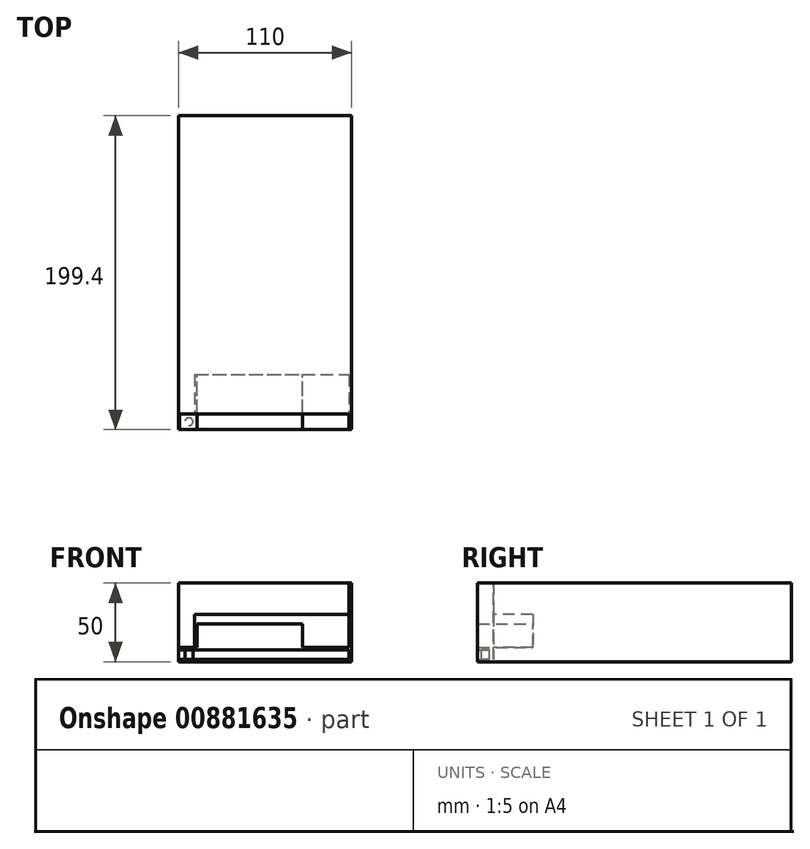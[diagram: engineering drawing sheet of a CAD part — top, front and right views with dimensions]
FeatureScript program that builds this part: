
annotation { "Feature Type Name" : "Feature", "Feature Type Description" : "" }
export const myFeature = defineFeature(function(context is Context, id is Id, definition is map)
    precondition{}
    {
        {
            var Q0;
            Q0=qCreatedBy(makeId("Front.planeOp"),FACE);
            var sketch = newSketch(context, id + "F0", { "sketchPlane" : qUnion([Q0])});
            skLineSegment(sketch, "E0.bottom", {"start": v(0, 0) * mm, "end": v(110, 0) * mm});
            skLineSegment(sketch, "E0.top", {"start": v(0, 50) * mm, "end": v(110, 50) * mm});
            skLineSegment(sketch, "E0.left", {"start": v(0, 0) * mm, "end": v(0, 50) * mm});
            skLineSegment(sketch, "E0.right", {"start": v(110, 0) * mm, "end": v(110, 50) * mm});
            skLineSegment(sketch, "E1", {"start": v(108.4, 50) * mm, "end": v(108.4, 0) * mm});
            skLineSegment(sketch, "E2", {"start": v(0, 9.2) * mm, "end": v(108.4, 9.2) * mm});
            skLineSegment(sketch, "E3", {"start": v(10.2, 50) * mm, "end": v(10.2, 9.2) * mm});
            skLineSegment(sketch, "E4", {"start": v(10.2, 30) * mm, "end": v(108.4, 30) * mm});
            skLineSegment(sketch, "E5", {"start": v(11.6, 9.2) * mm, "end": v(11.6, 24.1) * mm});
            skLineSegment(sketch, "E6", {"start": v(11.6, 24.1) * mm, "end": v(78.8, 24.1) * mm});
            skLineSegment(sketch, "E7", {"start": v(78.8, 24.1) * mm, "end": v(78.8, 9.2) * mm});
            skLineSegment(sketch, "E8", {"start": v(0, 7.6) * mm, "end": v(108.4, 7.6) * mm});
            skLineSegment(sketch, "E9", {"start": v(0, 1.6) * mm, "end": v(108.4, 1.6) * mm});
            skLineSegment(sketch, "E10", {"start": v(0.6, 0) * mm, "end": v(0.6, 50) * mm});
            skLineSegment(sketch, "E11", {"start": v(0, 49.4) * mm, "end": v(110, 49.4) * mm});
            skSolve(sketch);
        }
        {
            var Q0;
            {var subQ0=sQuery(id+"F0.wireOp",EDGE,"E1");var subQ1=sQuery(id+"F0.wireOp",EDGE,"E0.top");var subQ2=makeQuery(id+"F0.imprint","INTERSECT",VERTEX,{"derivedFrom":[subQ1,subQ0]});Q0=makeQuery(id+"F0.imprint","IMPRINT",FACE,{"disambiguationData":[TD([[makeQuery(id+"F0.imprint","IMPRINT",EDGE,{"disambiguationData":[TD([[subQ2,1.0]])],"derivedFrom":subQ1}),-1.0]])]});}
            var Q1;
            {var subQ0=sQuery(id+"F0.wireOp",EDGE,"E3");var subQ1=sQuery(id+"F0.wireOp",EDGE,"E0.top");var subQ2=makeQuery(id+"F0.imprint","INTERSECT",VERTEX,{"derivedFrom":[subQ1,subQ0]});Q1=makeQuery(id+"F0.imprint","IMPRINT",FACE,{"disambiguationData":[TD([[makeQuery(id+"F0.imprint","IMPRINT",EDGE,{"disambiguationData":[TD([[subQ2,1.0]])],"derivedFrom":subQ1}),-1.0]])]});}
            var Q2;
            {var subQ0=sQuery(id+"F0.wireOp",EDGE,"E2");var subQ1=sQuery(id+"F0.wireOp",EDGE,"E0.left");var subQ2=makeQuery(id+"F0.imprint","INTERSECT",VERTEX,{"derivedFrom":[subQ1,subQ0]});Q2=makeQuery(id+"F0.imprint","IMPRINT",FACE,{"disambiguationData":[TD([[makeQuery(id+"F0.imprint","IMPRINT",EDGE,{"disambiguationData":[TD([[subQ2,-1.0]])],"derivedFrom":subQ1}),-1.0]])]});}
            var Q3;
            {var subQ0=sQuery(id+"F0.wireOp",EDGE,"E2");var subQ1=sQuery(id+"F0.wireOp",EDGE,"E0.left");var subQ2=makeQuery(id+"F0.imprint","INTERSECT",VERTEX,{"derivedFrom":[subQ1,subQ0]});Q3=makeQuery(id+"F0.imprint","IMPRINT",FACE,{"disambiguationData":[TD([[makeQuery(id+"F0.imprint","IMPRINT",EDGE,{"disambiguationData":[TD([[subQ2,1.0]])],"derivedFrom":subQ1}),-1.0]])]});}
            var Q4;
            {var subQ0=sQuery(id+"F0.wireOp",EDGE,"E8");var subQ1=sQuery(id+"F0.wireOp",EDGE,"E0.left");var subQ2=makeQuery(id+"F0.imprint","INTERSECT",VERTEX,{"derivedFrom":[subQ1,subQ0]});Q4=makeQuery(id+"F0.imprint","IMPRINT",FACE,{"disambiguationData":[TD([[makeQuery(id+"F0.imprint","IMPRINT",EDGE,{"disambiguationData":[TD([[subQ2,1.0]])],"derivedFrom":subQ1}),-1.0]])]});}
            var Q5;
            {var subQ0=sQuery(id+"F0.wireOp",EDGE,"E0.left");var subQ1=sQuery(id+"F0.wireOp",EDGE,"E0.bottom");var subQ2=makeQuery(id+"F0.imprint","INTERSECT",VERTEX,{"derivedFrom":[subQ1,subQ0]});Q5=makeQuery(id+"F0.imprint","IMPRINT",FACE,{"disambiguationData":[TD([[makeQuery(id+"F0.imprint","IMPRINT",EDGE,{"disambiguationData":[TD([[subQ2,-1.0]])],"derivedFrom":subQ1}),1.0]])]});}
            var Q6;
            {var subQ0=sQuery(id+"F0.wireOp",EDGE,"E1");var subQ1=sQuery(id+"F0.wireOp",EDGE,"E0.bottom");var subQ2=makeQuery(id+"F0.imprint","INTERSECT",VERTEX,{"derivedFrom":[subQ1,subQ0]});Q6=makeQuery(id+"F0.imprint","IMPRINT",FACE,{"disambiguationData":[TD([[makeQuery(id+"F0.imprint","IMPRINT",EDGE,{"disambiguationData":[TD([[subQ2,1.0]])],"derivedFrom":subQ1}),1.0]])]});}
            var Q7;
            {var subQ5=sQuery(id+"F0.wireOp",EDGE,"E0.right");var subQ6=sQuery(id+"F0.wireOp",EDGE,"E0.bottom");var subQ7=makeQuery(id+"F0.imprint","INTERSECT",VERTEX,{"derivedFrom":[subQ6,subQ5]});Q7=makeQuery(id+"F0.imprint","IMPRINT",FACE,{"disambiguationData":[TD([[makeQuery(id+"F0.imprint","IMPRINT",EDGE,{"disambiguationData":[TD([[subQ7,1.0]])],"derivedFrom":subQ6}),1.0]])]});}
            var Q8;
            {var subQ0=sQuery(id+"F0.wireOp",EDGE,"E0.right");var subQ1=sQuery(id+"F0.wireOp",EDGE,"E0.top");var subQ2=makeQuery(id+"F0.imprint","INTERSECT",VERTEX,{"derivedFrom":[subQ1,subQ0]});Q8=makeQuery(id+"F0.imprint","IMPRINT",FACE,{"disambiguationData":[TD([[makeQuery(id+"F0.imprint","IMPRINT",EDGE,{"disambiguationData":[TD([[subQ2,1.0]])],"derivedFrom":subQ1}),-1.0]])]});}
            var Q9;
            {var subQ0=sQuery(id+"F0.wireOp",EDGE,"E0.left");var subQ1=sQuery(id+"F0.wireOp",EDGE,"E0.top");var subQ2=makeQuery(id+"F0.imprint","INTERSECT",VERTEX,{"derivedFrom":[subQ1,subQ0]});Q9=makeQuery(id+"F0.imprint","IMPRINT",FACE,{"disambiguationData":[TD([[makeQuery(id+"F0.imprint","IMPRINT",EDGE,{"disambiguationData":[TD([[subQ2,-1.0]])],"derivedFrom":subQ1}),-1.0]])]});}
            var Q10;
            {var subQ0=sQuery(id+"F0.wireOp",EDGE,"E2");var subQ7=sQuery(id+"F0.wireOp",EDGE,"E1");var subQ10=makeQuery(id+"F0.imprint","INTERSECT",VERTEX,{"derivedFrom":[subQ7,subQ0]});Q10=makeQuery(id+"F0.imprint","IMPRINT",FACE,{"disambiguationData":[TD([[makeQuery(id+"F0.imprint","IMPRINT",EDGE,{"disambiguationData":[TD([[subQ10,-1.0]])],"derivedFrom":subQ7}),-1.0]])]});}
            var Q11;
            {var subQ1=sQuery(id+"F0.wireOp",EDGE,"E2");var subQ5=sQuery(id+"F0.wireOp",EDGE,"E3");var subQ6=makeQuery(id+"F0.imprint","INTERSECT",VERTEX,{"derivedFrom":[subQ1,subQ5]});Q11=makeQuery(id+"F0.imprint","IMPRINT",FACE,{"disambiguationData":[TD([[makeQuery(id+"F0.imprint","IMPRINT",EDGE,{"disambiguationData":[TD([[subQ6,1.0]])],"derivedFrom":subQ1}),1.0]])]});}
            var Q12;
            {var subQ0=sQuery(id+"F0.wireOp",EDGE,"E4");Q12=makeQuery(id+"F0.imprint","IMPRINT",FACE,{"disambiguationData":[TD([[makeQuery(id+"F0.imprint","IMPRINT",EDGE,{"derivedFrom":subQ0}),1.0]])]});}
            var Q13;
            {var subQ6=sQuery(id+"F0.wireOp",EDGE,"E4");Q13=makeQuery(id+"F0.imprint","IMPRINT",FACE,{"disambiguationData":[TD([[makeQuery(id+"F0.imprint","IMPRINT",EDGE,{"derivedFrom":subQ6}),-1.0]])]});}
            var Q14;
            {var subQ0=sQuery(id+"F0.wireOp",EDGE,"E5");Q14=makeQuery(id+"F0.imprint","IMPRINT",FACE,{"disambiguationData":[TD([[makeQuery(id+"F0.imprint","IMPRINT",EDGE,{"derivedFrom":subQ0}),-1.0]])]});}
            var Q15;
            {var subQ0=sQuery(id+"F0.wireOp",EDGE,"E8");var subQ1=sQuery(id+"F0.wireOp",EDGE,"E1");var subQ2=makeQuery(id+"F0.imprint","INTERSECT",VERTEX,{"derivedFrom":[subQ1,subQ0]});Q15=makeQuery(id+"F0.imprint","IMPRINT",FACE,{"disambiguationData":[TD([[makeQuery(id+"F0.imprint","IMPRINT",EDGE,{"disambiguationData":[TD([[subQ2,-1.0]])],"derivedFrom":subQ1}),-1.0]])]});}
            extrude(context, id + "F1", {"entities" : qUnion([Q0, Q1, Q2, Q3, Q4, Q5, Q6, Q7, Q8, Q9, Q10, Q11, Q12, Q13, Q14, Q15]), "oppositeDirection" : true, "depth" : 189.4 * mm, "offsetDistance" : 25 * mm});
        }
        {
            var Q0;
            {var subQ0=sQuery(id+"F0.wireOp",EDGE,"E5");Q0=makeQuery(id+"F0.imprint","IMPRINT",FACE,{"disambiguationData":[TD([[makeQuery(id+"F0.imprint","IMPRINT",EDGE,{"derivedFrom":subQ0}),-1.0]])]});}
            var Q1;
            {var subQ5=sQuery(id+"F0.wireOp",EDGE,"E0.right");var subQ6=sQuery(id+"F0.wireOp",EDGE,"E0.bottom");var subQ7=makeQuery(id+"F0.imprint","INTERSECT",VERTEX,{"derivedFrom":[subQ6,subQ5]});Q1=makeQuery(id+"F0.imprint","IMPRINT",FACE,{"disambiguationData":[TD([[makeQuery(id+"F0.imprint","IMPRINT",EDGE,{"disambiguationData":[TD([[subQ7,1.0]])],"derivedFrom":subQ6}),1.0]])]});}
            var Q2;
            {var subQ0=sQuery(id+"F0.wireOp",EDGE,"E1");var subQ1=sQuery(id+"F0.wireOp",EDGE,"E0.bottom");var subQ2=makeQuery(id+"F0.imprint","INTERSECT",VERTEX,{"derivedFrom":[subQ1,subQ0]});Q2=makeQuery(id+"F0.imprint","IMPRINT",FACE,{"disambiguationData":[TD([[makeQuery(id+"F0.imprint","IMPRINT",EDGE,{"disambiguationData":[TD([[subQ2,1.0]])],"derivedFrom":subQ1}),1.0]])]});}
            var Q3;
            {var subQ0=sQuery(id+"F0.wireOp",EDGE,"E0.right");var subQ1=sQuery(id+"F0.wireOp",EDGE,"E0.top");var subQ2=makeQuery(id+"F0.imprint","INTERSECT",VERTEX,{"derivedFrom":[subQ1,subQ0]});Q3=makeQuery(id+"F0.imprint","IMPRINT",FACE,{"disambiguationData":[TD([[makeQuery(id+"F0.imprint","IMPRINT",EDGE,{"disambiguationData":[TD([[subQ2,1.0]])],"derivedFrom":subQ1}),-1.0]])]});}
            var Q4;
            {var subQ0=sQuery(id+"F0.wireOp",EDGE,"E0.left");var subQ1=sQuery(id+"F0.wireOp",EDGE,"E0.bottom");var subQ2=makeQuery(id+"F0.imprint","INTERSECT",VERTEX,{"derivedFrom":[subQ1,subQ0]});Q4=makeQuery(id+"F0.imprint","IMPRINT",FACE,{"disambiguationData":[TD([[makeQuery(id+"F0.imprint","IMPRINT",EDGE,{"disambiguationData":[TD([[subQ2,-1.0]])],"derivedFrom":subQ1}),1.0]])]});}
            var Q5;
            {var subQ0=sQuery(id+"F0.wireOp",EDGE,"E2");var subQ7=sQuery(id+"F0.wireOp",EDGE,"E1");var subQ10=makeQuery(id+"F0.imprint","INTERSECT",VERTEX,{"derivedFrom":[subQ7,subQ0]});Q5=makeQuery(id+"F0.imprint","IMPRINT",FACE,{"disambiguationData":[TD([[makeQuery(id+"F0.imprint","IMPRINT",EDGE,{"disambiguationData":[TD([[subQ10,-1.0]])],"derivedFrom":subQ7}),-1.0]])]});}
            extrude(context, id + "F2", {"entities" : qUnion([Q0, Q1, Q2, Q3, Q4, Q5]), "operationType" : NewBodyOperationType.ADD, "depth" : 10 * mm, "offsetDistance" : 25 * mm});
        }
        {
            var Q0;
            {var subQ6=sQuery(id+"F0.wireOp",EDGE,"E4");Q0=makeQuery(id+"F0.imprint","IMPRINT",FACE,{"disambiguationData":[TD([[makeQuery(id+"F0.imprint","IMPRINT",EDGE,{"derivedFrom":subQ6}),-1.0]])]});}
            extrude(context, id + "F3", {"entities" : qUnion([Q0]), "operationType" : NewBodyOperationType.REMOVE, "oppositeDirection" : true, "depth" : 25 * mm, "offsetDistance" : 25 * mm});
        }
        {
            var Q0;
            {var subQ0=sQuery(id+"F0.wireOp",EDGE,"E2");var subQ1=makeQuery(id+"F0.imprint","INTERSECT",VERTEX,{"derivedFrom":[subQ0,sQuery(id+"F0.wireOp",EDGE,"E3")]});var subQ2=makeQuery(id+"F0.imprint","IMPRINT",EDGE,{"disambiguationData":[TD([[subQ1,-1.0]])],"derivedFrom":subQ0});Q0=makeQuery(id+"F3.boolean.opBoolean","MERGE",FACE,{"derivedFrom":[makeQuery(id+"F2.opExtrude","SWEPT_FACE",FACE,{"disambiguationData":[OSD([subQ0]),TDD([makeQuery(id+"F0.imprint","IMPRINT",EDGE,{"disambiguationData":[TD([[subQ1,1.0]])],"derivedFrom":subQ0}),subQ2])]})],"fromTools":[makeQuery(id+"F3.opExtrude","SWEPT_FACE",FACE,{"disambiguationData":[OSD([subQ0]),TDD([subQ2])]})]});}
            var sketch = newSketch(context, id + "F4", { "sketchPlane" : qUnion([Q0])});
            skLineSegment(sketch, "E12.0.0", {"start": v(10.2, 0) * mm, "end": v(0.6, 0) * mm});
            skLineSegment(sketch, "E12.0.1", {"start": v(0.6, 0) * mm, "end": v(0.6, -10) * mm});
            skLineSegment(sketch, "E12.0.2", {"start": v(0.6, -10) * mm, "end": v(11.6, -10) * mm});
            skLineSegment(sketch, "E12.0.3", {"start": v(11.6, -10) * mm, "end": v(11.6, 25) * mm});
            skLineSegment(sketch, "E12.0.4", {"start": v(11.6, 25) * mm, "end": v(10.2, 25) * mm});
            skLineSegment(sketch, "E12.0.5", {"start": v(10.2, 25) * mm, "end": v(10.2, 0) * mm});
            skCircle(sketch, "E13", {"center": v(6.6, -5) * mm, "radius": 2.5 * mm});
            skSolve(sketch);
        }
        {
            var Q0;
            Q0=makeQuery(id+"F4.imprint","IMPRINT",FACE,{"disambiguationData":[TD([[makeQuery(id+"F4.imprint","IMPRINT",EDGE,{"derivedFrom":sQuery(id+"F4.wireOp",EDGE,"E13")}),1.0]])]});
            var Q1;
            Q1=makeQuery(id+"F2.opExtrude","SWEPT_FACE",FACE,{"disambiguationData":[OSD([sQuery(id+"F0.wireOp",EDGE,"E9")])]});
            extrude(context, id + "F5", {"entities" : qUnion([Q0]), "operationType" : NewBodyOperationType.ADD, "endBound" : BoundingType.UP_TO_SURFACE, "oppositeDirection" : true, "depth" : 25 * mm, "endBoundEntityFace" : qUnion([Q1]), "offsetDistance" : 25 * mm});
        }
    });
